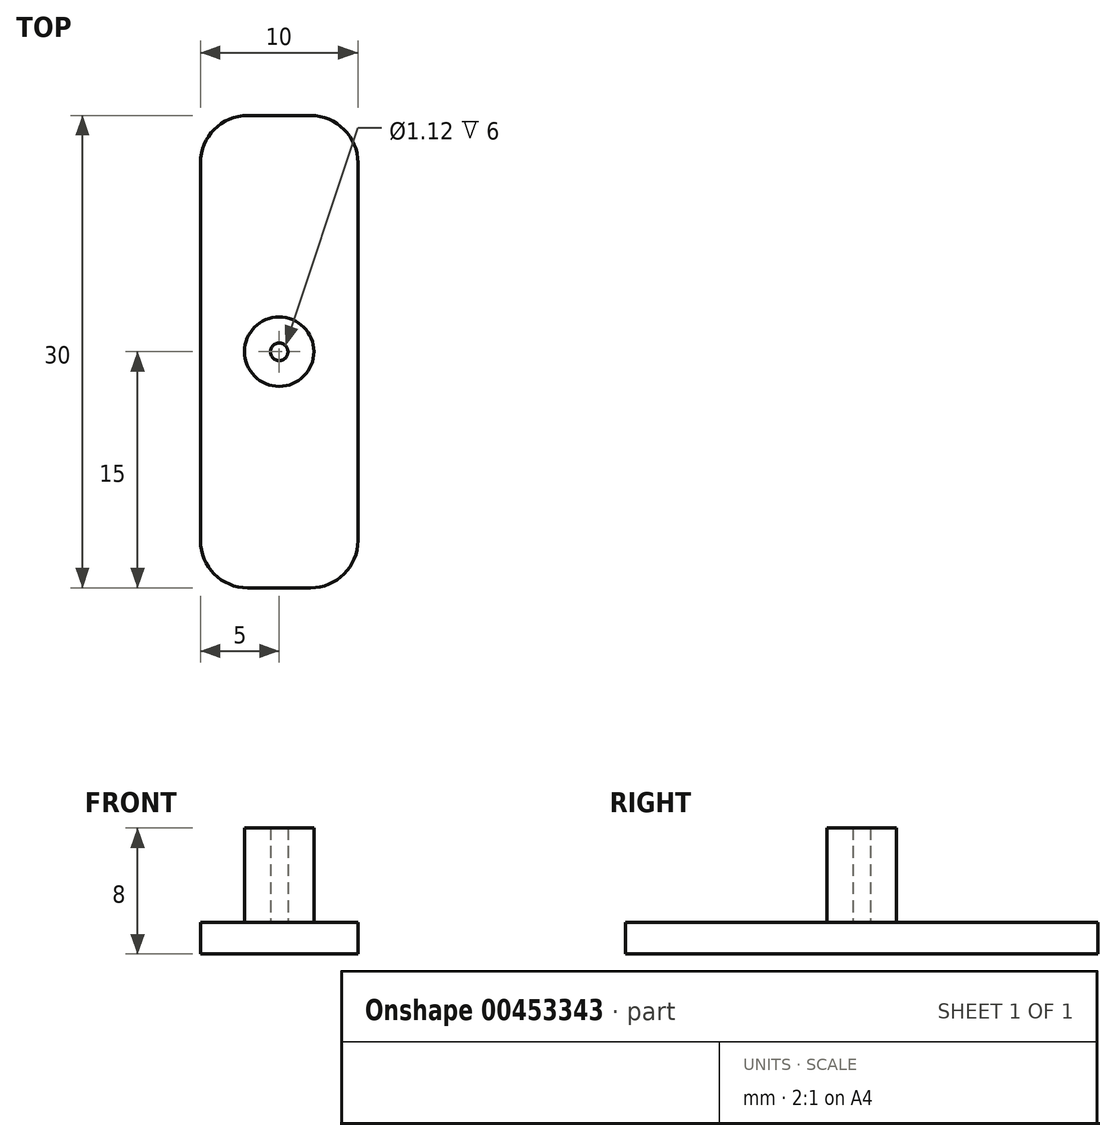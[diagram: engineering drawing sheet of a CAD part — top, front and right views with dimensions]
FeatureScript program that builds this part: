
annotation { "Feature Type Name" : "Feature", "Feature Type Description" : "" }
export const myFeature = defineFeature(function(context is Context, id is Id, definition is map)
    precondition{}
    {
        {
            var Q0;
            Q0=qCreatedBy(makeId("Top.planeOp"),FACE);
            var sketch = newSketch(context, id + "F0", { "sketchPlane" : qUnion([Q0])});
            skLineSegment(sketch, "E0.bottom", {"start": v(5, 15) * mm, "end": v(-5, 15) * mm});
            skLineSegment(sketch, "E0.top", {"start": v(5, -15) * mm, "end": v(-5, -15) * mm});
            skLineSegment(sketch, "E0.left", {"start": v(5, 15) * mm, "end": v(5, -15) * mm});
            skLineSegment(sketch, "E0.right", {"start": v(-5, 15) * mm, "end": v(-5, -15) * mm});
            skPoint(sketch, "E0.middle", {"position": v(0, 0) * mm});
            skSolve(sketch);
        }
        {
            var Q0;
            Q0 = qSketchRegion(id + "F0", true);
            extrude(context, id + "F1", {"entities" : qUnion([Q0]), "depth" : 2 * mm});
        }
        {
            var Q0;
            Q0=makeQuery(id+"F1.opExtrude","CAP_FACE",FACE,{"disambiguationData":[OSD([sQuery(id+"F0.wireOp",EDGE,"E0.bottom"),sQuery(id+"F0.wireOp",EDGE,"E0.top"),sQuery(id+"F0.wireOp",EDGE,"E0.left"),sQuery(id+"F0.wireOp",EDGE,"E0.right")])],"isStart":false});
            var sketch = newSketch(context, id + "F2", { "sketchPlane" : qUnion([Q0])});
            skCircle(sketch, "E1", {"center": v(0, 0) * mm, "radius": 2.2 * mm});
            skCircle(sketch, "E2", {"center": v(0, 0) * mm, "radius": 0.56 * mm});
            skSolve(sketch);
        }
        {
            var Q0;
            Q0 = qSketchRegion(id + "F2", true);
            extrude(context, id + "F3", {"entities" : qUnion([Q0]), "operationType" : NewBodyOperationType.ADD, "depth" : 6 * mm});
        }
        {
            var Q0;
            Q0=makeQuery(id+"F1.opExtrude","SWEPT_EDGE",EDGE,{"disambiguationData":[OSD([sQuery(id+"F0.wireOp",EDGE,"E0.bottom"),sQuery(id+"F0.wireOp",EDGE,"E0.left")])]});
            var Q1;
            Q1=makeQuery(id+"F1.opExtrude","SWEPT_EDGE",EDGE,{"disambiguationData":[OSD([sQuery(id+"F0.wireOp",EDGE,"E0.top"),sQuery(id+"F0.wireOp",EDGE,"E0.left")])]});
            var Q2;
            Q2=makeQuery(id+"F1.opExtrude","SWEPT_EDGE",EDGE,{"disambiguationData":[OSD([sQuery(id+"F0.wireOp",EDGE,"E0.top"),sQuery(id+"F0.wireOp",EDGE,"E0.right")])]});
            var Q3;
            Q3=makeQuery(id+"F1.opExtrude","SWEPT_EDGE",EDGE,{"disambiguationData":[OSD([sQuery(id+"F0.wireOp",EDGE,"E0.bottom"),sQuery(id+"F0.wireOp",EDGE,"E0.right")])]});
            fillet(context, id + "F4", {"entities" : qUnion([Q0, Q1, Q2, Q3]), "radius" : 3 * mm, "tangentPropagation" : true, "allowEdgeOverflow" : false});
        }
    });
